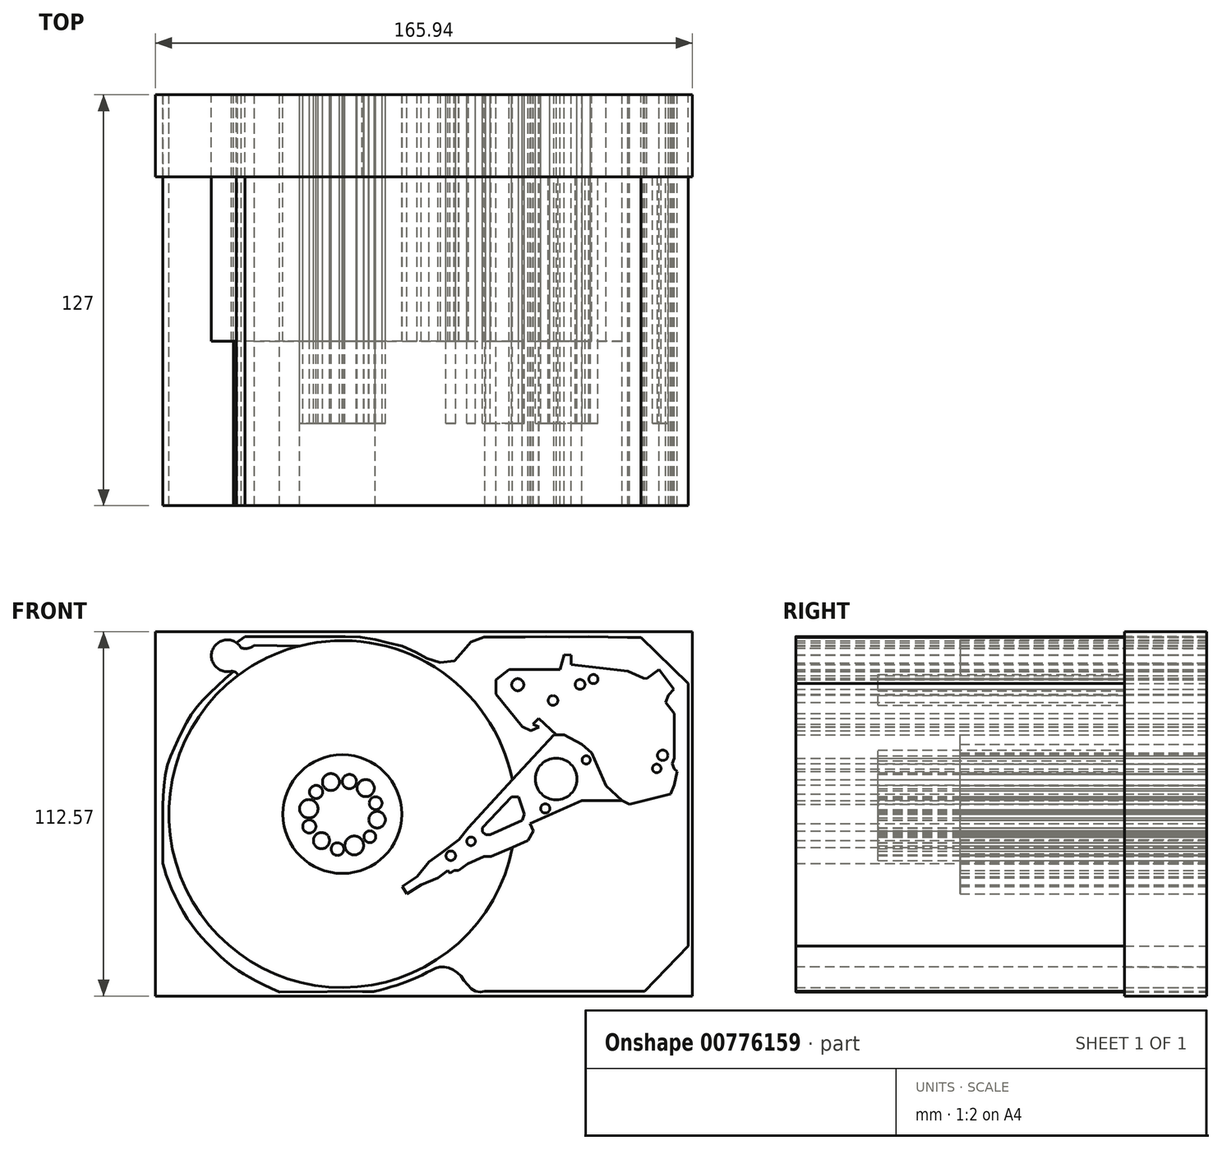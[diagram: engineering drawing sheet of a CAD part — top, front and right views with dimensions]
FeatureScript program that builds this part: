
annotation { "Feature Type Name" : "Feature", "Feature Type Description" : "" }
export const myFeature = defineFeature(function(context is Context, id is Id, definition is map)
    precondition{}
    {
        {
            var Q0;
            Q0=qCreatedBy(makeId("Front.planeOp"),FACE);
            var sketch = newSketch(context, id + "F0", { "sketchPlane" : qUnion([Q0])});
            skLineSegment(sketch, "E0.bottom", {"start": v(-166.9, -0.39) * mm, "end": v(-0.96, -0.39) * mm});
            skLineSegment(sketch, "E0.top", {"start": v(-166.9, -112.96) * mm, "end": v(-0.96, -112.96) * mm});
            skLineSegment(sketch, "E0.right", {"start": v(-0.96, -0.39) * mm, "end": v(-0.96, -112.96) * mm});
            skCircle(sketch, "E1", {"center": v(-109.14, -56.73) * mm, "radius": 53.62 * mm});
            skCircle(sketch, "E2", {"center": v(-109.14, -56.73) * mm, "radius": 18.36 * mm});
            skCircle(sketch, "E3", {"center": v(-144.7, -7.8) * mm, "radius": 2.3 * mm});
            skCircle(sketch, "E4", {"center": v(-144.7, -7.8) * mm, "radius": 4.92 * mm});
            skFitSpline(sketch, "E5", {"points": [v(-143.4, -12.55) * mm, v(-141.85, -13.06) * mm, v(-141.48, -13.95) * mm], "startDerivative": vector(3.27, -0.6) * mm, "endDerivative": vector(0.52, -2.37) * mm});
            skLineSegment(sketch, "E6", {"start": v(-136.28, -4.54) * mm, "end": v(-122.34, -4.75) * mm});
            skFitSpline(sketch, "E7", {"points": [v(-136.28, -4.54) * mm, v(-138.28, -5.49) * mm, v(-140.4, -5.42) * mm], "startDerivative": vector(-3.87, -2.38) * mm, "endDerivative": vector(-4.35, 0.64) * mm});
            skLineSegment(sketch, "E8", {"start": v(-56.57, -46.13) * mm, "end": v(-70.2, -60.97) * mm});
            skLineSegment(sketch, "E9", {"start": v(-70.2, -60.97) * mm, "end": v(-73.07, -64.56) * mm});
            skLineSegment(sketch, "E10", {"start": v(-73.07, -64.56) * mm, "end": v(-78.81, -68.99) * mm});
            skLineSegment(sketch, "E11", {"start": v(-78.81, -68.99) * mm, "end": v(-82.4, -71.5) * mm});
            skLineSegment(sketch, "E12", {"start": v(-82.4, -71.5) * mm, "end": v(-86, -76.05) * mm});
            skLineSegment(sketch, "E13", {"start": v(-86, -76.05) * mm, "end": v(-90.66, -79.04) * mm});
            skLineSegment(sketch, "E14", {"start": v(-90.66, -79.04) * mm, "end": v(-89.15, -81.39) * mm});
            skLineSegment(sketch, "E15", {"start": v(-89.15, -81.39) * mm, "end": v(-84.8, -78.6) * mm});
            skLineSegment(sketch, "E16", {"start": v(-84.8, -78.6) * mm, "end": v(-79.6, -76.39) * mm});
            skLineSegment(sketch, "E17", {"start": v(-79.6, -76.39) * mm, "end": v(-75.84, -73.6) * mm});
            skLineSegment(sketch, "E18", {"start": v(-75.84, -73.6) * mm, "end": v(-70.2, -69) * mm});
            skLineSegment(sketch, "E19", {"start": v(-70.2, -69) * mm, "end": v(-65.06, -66.97) * mm});
            skLineSegment(sketch, "E20", {"start": v(-65.06, -66.97) * mm, "end": v(-63.32, -67.57) * mm});
            skLineSegment(sketch, "E21", {"start": v(-63.32, -67.57) * mm, "end": v(-61.59, -66.81) * mm});
            skLineSegment(sketch, "E22", {"start": v(-61.59, -66.81) * mm, "end": v(-61.59, -65.46) * mm});
            skLineSegment(sketch, "E23", {"start": v(-61.59, -65.46) * mm, "end": v(-55.87, -62.92) * mm});
            skLineSegment(sketch, "E24", {"start": v(-76.54, -74.12) * mm, "end": v(-75.84, -75.07) * mm});
            skLineSegment(sketch, "E25", {"start": v(-75.84, -75.07) * mm, "end": v(-74.56, -74.12) * mm});
            skLineSegment(sketch, "E26", {"start": v(-74.56, -74.12) * mm, "end": v(-73.2, -74.12) * mm});
            skLineSegment(sketch, "E27", {"start": v(-73.2, -74.12) * mm, "end": v(-70.44, -72.08) * mm});
            skLineSegment(sketch, "E28", {"start": v(-70.44, -72.08) * mm, "end": v(-65.36, -69.83) * mm});
            skLineSegment(sketch, "E29", {"start": v(-65.36, -69.83) * mm, "end": v(-63.17, -69.83) * mm});
            skLineSegment(sketch, "E30", {"start": v(-63.17, -69.83) * mm, "end": v(-56.5, -66.97) * mm});
            skCircle(sketch, "E31", {"center": v(-69.35, -65.16) * mm, "radius": 1.33 * mm});
            skCircle(sketch, "E32", {"center": v(-75.6, -69.6) * mm, "radius": 1.49 * mm});
            skLineSegment(sketch, "E33", {"start": v(-65.8, -60.94) * mm, "end": v(-65.8, -62.22) * mm});
            skLineSegment(sketch, "E34", {"start": v(-65.8, -62.22) * mm, "end": v(-64.86, -63.09) * mm});
            skLineSegment(sketch, "E35", {"start": v(-64.86, -63.09) * mm, "end": v(-63.4, -63.09) * mm});
            skLineSegment(sketch, "E36", {"start": v(-63.4, -63.09) * mm, "end": v(-53.52, -58.67) * mm});
            skLineSegment(sketch, "E37", {"start": v(-53.52, -58.67) * mm, "end": v(-52.93, -56.78) * mm});
            skLineSegment(sketch, "E38", {"start": v(-52.93, -56.78) * mm, "end": v(-54.63, -51.36) * mm});
            skLineSegment(sketch, "E39", {"start": v(-54.63, -51.36) * mm, "end": v(-56.84, -51.36) * mm});
            skLineSegment(sketch, "E40", {"start": v(-56.84, -51.36) * mm, "end": v(-65.8, -60.94) * mm});
            skLineSegment(sketch, "E41", {"start": v(-56.5, -66.97) * mm, "end": v(-51.76, -64.87) * mm});
            skLineSegment(sketch, "E42", {"start": v(-51.76, -64.87) * mm, "end": v(-50.07, -61.98) * mm});
            skLineSegment(sketch, "E43", {"start": v(-50.07, -61.98) * mm, "end": v(-51.1, -59.68) * mm});
            skLineSegment(sketch, "E44", {"start": v(-51.1, -59.68) * mm, "end": v(-35.05, -52.56) * mm});
            skLineSegment(sketch, "E45", {"start": v(-35.05, -52.56) * mm, "end": v(-22.63, -52.56) * mm});
            skLineSegment(sketch, "E46", {"start": v(-22.63, -52.56) * mm, "end": v(-27.56, -48.04) * mm});
            skLineSegment(sketch, "E47", {"start": v(-27.56, -48.04) * mm, "end": v(-30.07, -42.36) * mm});
            skLineSegment(sketch, "E48", {"start": v(-30.07, -42.36) * mm, "end": v(-32.1, -37.8) * mm});
            skLineSegment(sketch, "E49", {"start": v(-32.1, -37.8) * mm, "end": v(-35.05, -35.1) * mm});
            skLineSegment(sketch, "E50", {"start": v(-35.05, -35.1) * mm, "end": v(-40.6, -32.18) * mm});
            skLineSegment(sketch, "E51", {"start": v(-40.6, -32.18) * mm, "end": v(-42.98, -32.18) * mm});
            skLineSegment(sketch, "E52", {"start": v(-42.98, -32.18) * mm, "end": v(-50.16, -25.59) * mm});
            skLineSegment(sketch, "E53", {"start": v(-50.16, -25.59) * mm, "end": v(-45, -14.06) * mm});
            skLineSegment(sketch, "E54", {"start": v(-45, -14.06) * mm, "end": v(-42.48, -14.53) * mm});
            skLineSegment(sketch, "E55", {"start": v(-42.48, -14.53) * mm, "end": v(-40.6, -7.44) * mm});
            skLineSegment(sketch, "E56", {"start": v(-40.6, -7.44) * mm, "end": v(-38.38, -7.59) * mm});
            skLineSegment(sketch, "E57", {"start": v(-38.38, -7.59) * mm, "end": v(-38.38, -10.58) * mm});
            skLineSegment(sketch, "E58", {"start": v(-38.38, -10.58) * mm, "end": v(-35.05, -10.95) * mm});
            skLineSegment(sketch, "E59", {"start": v(-35.05, -10.95) * mm, "end": v(-20.88, -12.51) * mm});
            skLineSegment(sketch, "E60", {"start": v(-20.88, -12.51) * mm, "end": v(-17.41, -14.06) * mm});
            skLineSegment(sketch, "E61", {"start": v(-17.41, -14.06) * mm, "end": v(-16.06, -14.67) * mm});
            skLineSegment(sketch, "E62", {"start": v(-16.06, -14.67) * mm, "end": v(-15.01, -14.8) * mm});
            skLineSegment(sketch, "E63", {"start": v(-15.01, -14.8) * mm, "end": v(-11.17, -12) * mm});
            skLineSegment(sketch, "E64", {"start": v(-11.17, -12) * mm, "end": v(-6.7, -18.11) * mm});
            skLineSegment(sketch, "E65", {"start": v(-6.7, -18.11) * mm, "end": v(-8.27, -19.97) * mm});
            skLineSegment(sketch, "E66", {"start": v(-8.27, -19.97) * mm, "end": v(-9.25, -22.16) * mm});
            skLineSegment(sketch, "E67", {"start": v(-9.25, -22.16) * mm, "end": v(-6.48, -25.59) * mm});
            skLineSegment(sketch, "E68", {"start": v(-6.48, -25.59) * mm, "end": v(-6.48, -39.43) * mm});
            skLineSegment(sketch, "E69", {"start": v(-6.48, -39.43) * mm, "end": v(-7.21, -41.08) * mm});
            skLineSegment(sketch, "E70", {"start": v(-7.21, -41.08) * mm, "end": v(-6.48, -42.74) * mm});
            skLineSegment(sketch, "E71", {"start": v(-6.48, -42.74) * mm, "end": v(-5.62, -43.53) * mm});
            skLineSegment(sketch, "E72", {"start": v(-5.62, -43.53) * mm, "end": v(-6.48, -47.71) * mm});
            skLineSegment(sketch, "E73", {"start": v(-6.48, -47.71) * mm, "end": v(-7.71, -50.47) * mm});
            skLineSegment(sketch, "E74", {"start": v(-7.71, -50.47) * mm, "end": v(-20.32, -53.75) * mm});
            skLineSegment(sketch, "E75", {"start": v(-20.32, -53.75) * mm, "end": v(-22.63, -52.56) * mm});
            skLineSegment(sketch, "E76", {"start": v(-48.5, -27.12) * mm, "end": v(-50.16, -28.93) * mm});
            skLineSegment(sketch, "E77", {"start": v(-50.16, -28.93) * mm, "end": v(-48.3, -29.77) * mm});
            skLineSegment(sketch, "E78", {"start": v(-48.3, -29.77) * mm, "end": v(-50.88, -30.91) * mm});
            skLineSegment(sketch, "E79", {"start": v(-50.88, -30.91) * mm, "end": v(-53.52, -29.73) * mm});
            skLineSegment(sketch, "E80", {"start": v(-53.52, -29.73) * mm, "end": v(-61.64, -19.67) * mm});
            skLineSegment(sketch, "E81", {"start": v(-61.64, -19.67) * mm, "end": v(-61.64, -15.24) * mm});
            skLineSegment(sketch, "E82", {"start": v(-61.64, -15.24) * mm, "end": v(-57.63, -12) * mm});
            skLineSegment(sketch, "E83", {"start": v(-57.63, -12) * mm, "end": v(-41.81, -12) * mm});
            skCircle(sketch, "E84", {"center": v(-54.91, -16.75) * mm, "radius": 1.86 * mm});
            skCircle(sketch, "E85", {"center": v(-44, -21.6) * mm, "radius": 1.5 * mm});
            skCircle(sketch, "E86", {"center": v(-35.65, -16.67) * mm, "radius": 1.53 * mm});
            skCircle(sketch, "E87", {"center": v(-31.51, -15) * mm, "radius": 1.42 * mm});
            skCircle(sketch, "E88", {"center": v(-10.1, -38.56) * mm, "radius": 1.62 * mm});
            skCircle(sketch, "E89", {"center": v(-11.93, -42.62) * mm, "radius": 1.32 * mm});
            skCircle(sketch, "E90", {"center": v(-43.03, -45.89) * mm, "radius": 6.45 * mm});
            skCircle(sketch, "E91", {"center": v(-46.4, -55) * mm, "radius": 1.43 * mm});
            skCircle(sketch, "E92", {"center": v(-33.75, -39.98) * mm, "radius": 1.28 * mm});
            skLineSegment(sketch, "E93", {"start": v(-56.57, -46.13) * mm, "end": v(-43.77, -32.18) * mm});
            skFitSpline(sketch, "E94", {"points": [v(-80.33, -11.5) * mm, v(-73.17, -10.43) * mm, v(-69.1, -6.07) * mm, v(-62.2, -5.02) * mm], "startDerivative": vector(23.42, -0.5) * mm, "endDerivative": vector(22.9, -0.58) * mm});
            skLineSegment(sketch, "E95", {"start": v(-62.2, -5.02) * mm, "end": v(-18.18, -5.02) * mm});
            skLineSegment(sketch, "E96", {"start": v(-18.18, -5.02) * mm, "end": v(-4.36, -18.7) * mm});
            skLineSegment(sketch, "E97", {"start": v(-4.36, -18.7) * mm, "end": v(-4.36, -66.47) * mm});
            skFitSpline(sketch, "E98", {"points": [v(-164.6, -71.95) * mm, v(-164.6, -66.7) * mm, v(-164.6, -59.04) * mm, v(-164.6, -51.95) * mm, v(-163.2, -41.7) * mm, v(-160.1, -34.16) * mm, v(-156.17, -26.51) * mm, v(-150.65, -19.87) * mm, v(-142.78, -12.66) * mm], "startDerivative": vector(-0.1, 49.54) * mm, "endDerivative": vector(57.81, 50.96) * mm});
            skFitSpline(sketch, "E99", {"points": [v(-139.28, -1.86) * mm, v(-130.4, -1.86) * mm, v(-117.22, -1.86) * mm, v(-110.36, -1.86) * mm, v(-105.97, -1.86) * mm, v(-100.34, -2.42) * mm, v(-96.51, -3.44) * mm, v(-91.9, -4.45) * mm, v(-87.17, -6.36) * mm, v(-83.68, -8.28) * mm, v(-80.08, -9.63) * mm, v(-75.13, -9.74) * mm, v(-71.98, -6.59) * mm, v(-70.08, -4.18) * mm, v(-67.7, -2.4) * mm, v(-58.27, -2.04) * mm, v(-49.57, -1.92) * mm, v(-38, -2.04) * mm, v(-29.64, -1.92) * mm, v(-20.94, -2.19) * mm, v(-16.12, -1.92) * mm], "startDerivative": vector(136.2, -0.04) * mm, "endDerivative": vector(98.93, 8.93) * mm});
            skLineSegment(sketch, "E100", {"start": v(-20.94, -2.19) * mm, "end": v(-16.78, -2.19) * mm});
            skLineSegment(sketch, "E101", {"start": v(-16.78, -2.19) * mm, "end": v(-2.18, -16.35) * mm});
            skLineSegment(sketch, "E102", {"start": v(-2.18, -16.35) * mm, "end": v(-2.18, -97.56) * mm});
            skLineSegment(sketch, "E103", {"start": v(-2.18, -97.56) * mm, "end": v(-15.7, -111.5) * mm});
            skLineSegment(sketch, "E104", {"start": v(-15.7, -111.5) * mm, "end": v(-65.04, -111.5) * mm});
            skFitSpline(sketch, "E105", {"points": [v(-65.04, -111.5) * mm, v(-67.97, -111.5) * mm, v(-70.81, -109.01) * mm, v(-73.18, -106.08) * mm, v(-75.92, -104.38) * mm, v(-78.87, -103.98) * mm, v(-81.18, -104.78) * mm, v(-84.59, -106.49) * mm, v(-91, -109.2) * mm, v(-94.82, -110.3) * mm, v(-99.01, -111.5) * mm, v(-103.47, -111.5) * mm], "startDerivative": vector(-37.68, -6.43) * mm, "endDerivative": vector(-45.54, 3.55) * mm});
            skLineSegment(sketch, "E106", {"start": v(-99.01, -111.5) * mm, "end": v(-128.6, -111.75) * mm});
            skLineSegment(sketch, "E107", {"start": v(-43.77, -32.18) * mm, "end": v(-42.98, -32.18) * mm});
            skCircle(sketch, "E108", {"center": v(-112.66, -46.82) * mm, "radius": 2.63 * mm});
            skCircle(sketch, "E109", {"center": v(-106.95, -46.67) * mm, "radius": 2.2 * mm});
            skCircle(sketch, "E110", {"center": v(-101.91, -48.7) * mm, "radius": 2.65 * mm});
            skCircle(sketch, "E111", {"center": v(-98.83, -53.36) * mm, "radius": 1.98 * mm});
            skCircle(sketch, "E112", {"center": v(-98.38, -58.47) * mm, "radius": 2.57 * mm});
            skCircle(sketch, "E113", {"center": v(-100.64, -63.73) * mm, "radius": 1.83 * mm});
            skCircle(sketch, "E114", {"center": v(-105.45, -66.43) * mm, "radius": 2.9 * mm});
            skCircle(sketch, "E115", {"center": v(-110.63, -67.56) * mm, "radius": 1.96 * mm});
            skCircle(sketch, "E116", {"center": v(-115.59, -64.93) * mm, "radius": 2.5 * mm});
            skCircle(sketch, "E117", {"center": v(-119.34, -60.57) * mm, "radius": 2.04 * mm});
            skCircle(sketch, "E118", {"center": v(-119.5, -55.09) * mm, "radius": 2.86 * mm});
            skCircle(sketch, "E119", {"center": v(-117.24, -49.9) * mm, "radius": 2.03 * mm});
            skLineSegment(sketch, "E120", {"start": v(-166.9, -0.39) * mm, "end": v(-166.9, -112.96) * mm});
            skLineSegment(sketch, "E121", {"start": v(-143.4, -12.55) * mm, "end": v(-142.78, -12.66) * mm});
            skLineSegment(sketch, "E122", {"start": v(-139.28, -1.86) * mm, "end": v(-141.93, -3.73) * mm});
            skFitSpline(sketch, "E123", {"points": [v(-164.6, -71.95) * mm, v(-162.75, -77.8) * mm, v(-157.8, -87.86) * mm, v(-152.23, -95.23) * mm, v(-143.52, -103.56) * mm, v(-138.11, -107.02) * mm, v(-128.6, -111.75) * mm], "startDerivative": vector(10.62, -39.33) * mm, "endDerivative": vector(57.28, -25) * mm});
            skSolve(sketch);
        }
        {
            var Q0;
            Q0 = qSketchRegion(id + "F0", true);
            extrude(context, id + "F1", {"entities" : qUnion([Q0]), "depth" : 25.4 * mm, "offsetDistance" : 25.4 * mm});
        }
        {
            var Q0;
            Q0=makeQuery(id+"F0.imprint","IMPRINT",FACE,{"disambiguationData":[TD([[makeQuery(id+"F0.imprint","IMPRINT",EDGE,{"derivedFrom":sQuery(id+"F0.wireOp",EDGE,"E2")}),-1.0]])]});
            var Q1;
            Q1=makeQuery(id+"F0.imprint","IMPRINT",FACE,{"disambiguationData":[TD([[makeQuery(id+"F0.imprint","IMPRINT",EDGE,{"derivedFrom":sQuery(id+"F0.wireOp",EDGE,"HnRhpPPG-Nzn8-Kiqb-eVUc-xORakVnLolAv")}),1.0]])]});
            var Q2;
            Q2=makeQuery(id+"F0.imprint","IMPRINT",FACE,{"disambiguationData":[TD([[makeQuery(id+"F0.imprint","IMPRINT",EDGE,{"derivedFrom":sQuery(id+"F0.wireOp",EDGE,"E46")}),-1.0]])]});
            var Q3;
            {var subQ3=sQuery(id+"F0.wireOp",EDGE,"E53");Q3=makeQuery(id+"F0.imprint","IMPRINT",FACE,{"disambiguationData":[TD([[makeQuery(id+"F0.imprint","IMPRINT",EDGE,{"derivedFrom":subQ3}),1.0]])]});}
            extrude(context, id + "F2", {"entities" : qUnion([Q0, Q1, Q2, Q3]), "operationType" : NewBodyOperationType.ADD, "depth" : 25.4 * mm, "offsetDistance" : 25.4 * mm});
        }
        {
            var Q0;
            Q0=makeQuery(id+"F0.imprint","IMPRINT",FACE,{"disambiguationData":[TD([[makeQuery(id+"F0.imprint","IMPRINT",EDGE,{"derivedFrom":sQuery(id+"F0.wireOp",EDGE,"E117")}),1.0]])]});
            var Q1;
            Q1=makeQuery(id+"F0.imprint","IMPRINT",FACE,{"disambiguationData":[TD([[makeQuery(id+"F0.imprint","IMPRINT",EDGE,{"derivedFrom":sQuery(id+"F0.wireOp",EDGE,"E118")}),1.0]])]});
            var Q2;
            Q2=makeQuery(id+"F0.imprint","IMPRINT",FACE,{"disambiguationData":[TD([[makeQuery(id+"F0.imprint","IMPRINT",EDGE,{"derivedFrom":sQuery(id+"F0.wireOp",EDGE,"E119")}),1.0]])]});
            var Q3;
            Q3=makeQuery(id+"F0.imprint","IMPRINT",FACE,{"disambiguationData":[TD([[makeQuery(id+"F0.imprint","IMPRINT",EDGE,{"derivedFrom":sQuery(id+"F0.wireOp",EDGE,"E108")}),1.0]])]});
            var Q4;
            Q4=makeQuery(id+"F0.imprint","IMPRINT",FACE,{"disambiguationData":[TD([[makeQuery(id+"F0.imprint","IMPRINT",EDGE,{"derivedFrom":sQuery(id+"F0.wireOp",EDGE,"E109")}),1.0]])]});
            var Q5;
            Q5=makeQuery(id+"F0.imprint","IMPRINT",FACE,{"disambiguationData":[TD([[makeQuery(id+"F0.imprint","IMPRINT",EDGE,{"derivedFrom":sQuery(id+"F0.wireOp",EDGE,"E110")}),1.0]])]});
            var Q6;
            Q6=makeQuery(id+"F0.imprint","IMPRINT",FACE,{"disambiguationData":[TD([[makeQuery(id+"F0.imprint","IMPRINT",EDGE,{"derivedFrom":sQuery(id+"F0.wireOp",EDGE,"E111")}),1.0]])]});
            var Q7;
            Q7=makeQuery(id+"F0.imprint","IMPRINT",FACE,{"disambiguationData":[TD([[makeQuery(id+"F0.imprint","IMPRINT",EDGE,{"derivedFrom":sQuery(id+"F0.wireOp",EDGE,"E112")}),1.0]])]});
            var Q8;
            Q8=makeQuery(id+"F0.imprint","IMPRINT",FACE,{"disambiguationData":[TD([[makeQuery(id+"F0.imprint","IMPRINT",EDGE,{"derivedFrom":sQuery(id+"F0.wireOp",EDGE,"E113")}),1.0]])]});
            var Q9;
            Q9=makeQuery(id+"F0.imprint","IMPRINT",FACE,{"disambiguationData":[TD([[makeQuery(id+"F0.imprint","IMPRINT",EDGE,{"derivedFrom":sQuery(id+"F0.wireOp",EDGE,"E114")}),1.0]])]});
            var Q10;
            Q10=makeQuery(id+"F0.imprint","IMPRINT",FACE,{"disambiguationData":[TD([[makeQuery(id+"F0.imprint","IMPRINT",EDGE,{"derivedFrom":sQuery(id+"F0.wireOp",EDGE,"E115")}),1.0]])]});
            var Q11;
            Q11=makeQuery(id+"F0.imprint","IMPRINT",FACE,{"disambiguationData":[TD([[makeQuery(id+"F0.imprint","IMPRINT",EDGE,{"derivedFrom":sQuery(id+"F0.wireOp",EDGE,"E116")}),1.0]])]});
            var Q12;
            Q12=makeQuery(id+"F0.imprint","IMPRINT",FACE,{"disambiguationData":[TD([[makeQuery(id+"F0.imprint","IMPRINT",EDGE,{"derivedFrom":sQuery(id+"F0.wireOp",EDGE,"E33")}),1.0]])]});
            var Q13;
            {var subQ1=sQuery(id+"F0.wireOp",EDGE,"E37");Q13=makeQuery(id+"F0.imprint","IMPRINT",FACE,{"disambiguationData":[TD([[makeQuery(id+"F0.imprint","IMPRINT",EDGE,{"derivedFrom":subQ1}),1.0]])]});}
            var Q14;
            Q14=makeQuery(id+"F0.imprint","IMPRINT",FACE,{"disambiguationData":[TD([[makeQuery(id+"F0.imprint","IMPRINT",EDGE,{"derivedFrom":sQuery(id+"F0.wireOp",EDGE,"E91")}),1.0]])]});
            var Q15;
            Q15=makeQuery(id+"F0.imprint","IMPRINT",FACE,{"disambiguationData":[TD([[makeQuery(id+"F0.imprint","IMPRINT",EDGE,{"derivedFrom":sQuery(id+"F0.wireOp",EDGE,"E90")}),1.0]])]});
            var Q16;
            Q16=makeQuery(id+"F0.imprint","IMPRINT",FACE,{"disambiguationData":[TD([[makeQuery(id+"F0.imprint","IMPRINT",EDGE,{"derivedFrom":sQuery(id+"F0.wireOp",EDGE,"E92")}),1.0]])]});
            var Q17;
            Q17=makeQuery(id+"F0.imprint","IMPRINT",FACE,{"disambiguationData":[TD([[makeQuery(id+"F0.imprint","IMPRINT",EDGE,{"derivedFrom":sQuery(id+"F0.wireOp",EDGE,"E32")}),1.0]])]});
            var Q18;
            Q18=makeQuery(id+"F0.imprint","IMPRINT",FACE,{"disambiguationData":[TD([[makeQuery(id+"F0.imprint","IMPRINT",EDGE,{"derivedFrom":sQuery(id+"F0.wireOp",EDGE,"E31")}),1.0]])]});
            var Q19;
            Q19=makeQuery(id+"F0.imprint","IMPRINT",FACE,{"disambiguationData":[TD([[makeQuery(id+"F0.imprint","IMPRINT",EDGE,{"derivedFrom":sQuery(id+"F0.wireOp",EDGE,"E84")}),1.0]])]});
            var Q20;
            Q20=makeQuery(id+"F0.imprint","IMPRINT",FACE,{"disambiguationData":[TD([[makeQuery(id+"F0.imprint","IMPRINT",EDGE,{"derivedFrom":sQuery(id+"F0.wireOp",EDGE,"E85")}),1.0]])]});
            var Q21;
            Q21=makeQuery(id+"F0.imprint","IMPRINT",FACE,{"disambiguationData":[TD([[makeQuery(id+"F0.imprint","IMPRINT",EDGE,{"derivedFrom":sQuery(id+"F0.wireOp",EDGE,"E86")}),1.0]])]});
            var Q22;
            Q22=makeQuery(id+"F0.imprint","IMPRINT",FACE,{"disambiguationData":[TD([[makeQuery(id+"F0.imprint","IMPRINT",EDGE,{"derivedFrom":sQuery(id+"F0.wireOp",EDGE,"E87")}),1.0]])]});
            var Q23;
            Q23=makeQuery(id+"F0.imprint","IMPRINT",FACE,{"disambiguationData":[TD([[makeQuery(id+"F0.imprint","IMPRINT",EDGE,{"derivedFrom":sQuery(id+"F0.wireOp",EDGE,"E88")}),1.0]])]});
            var Q24;
            Q24=makeQuery(id+"F0.imprint","IMPRINT",FACE,{"disambiguationData":[TD([[makeQuery(id+"F0.imprint","IMPRINT",EDGE,{"derivedFrom":sQuery(id+"F0.wireOp",EDGE,"E89")}),1.0]])]});
            extrude(context, id + "F3", {"entities" : qUnion([Q0, Q1, Q2, Q3, Q4, Q5, Q6, Q7, Q8, Q9, Q10, Q11, Q12, Q13, Q14, Q15, Q16, Q17, Q18, Q19, Q20, Q21, Q22, Q23, Q24]), "operationType" : NewBodyOperationType.ADD, "depth" : 101.6 * mm, "offsetDistance" : 25.4 * mm});
        }
        {
            var Q0;
            Q0=makeQuery(id+"F0.imprint","IMPRINT",FACE,{"disambiguationData":[TD([[makeQuery(id+"F0.imprint","IMPRINT",EDGE,{"derivedFrom":sQuery(id+"F0.wireOp",EDGE,"E2")}),1.0]])]});
            var Q1;
            {var subQ1=sQuery(id+"F0.wireOp",EDGE,"E37");Q1=makeQuery(id+"F0.imprint","IMPRINT",FACE,{"disambiguationData":[TD([[makeQuery(id+"F0.imprint","IMPRINT",EDGE,{"derivedFrom":subQ1}),-1.0]])]});}
            var Q2;
            {var subQ5=sQuery(id+"F0.wireOp",EDGE,"E8");Q2=makeQuery(id+"F0.imprint","IMPRINT",FACE,{"disambiguationData":[TD([[makeQuery(id+"F0.imprint","IMPRINT",EDGE,{"derivedFrom":subQ5}),1.0]])]});}
            var Q3;
            {var subQ4=sQuery(id+"F0.wireOp",EDGE,"E18");Q3=makeQuery(id+"F0.imprint","IMPRINT",FACE,{"disambiguationData":[TD([[makeQuery(id+"F0.imprint","IMPRINT",EDGE,{"derivedFrom":subQ4}),-1.0]])]});}
            var Q4;
            {var subQ0=sQuery(id+"F0.wireOp",EDGE,"E6");Q4=makeQuery(id+"F0.imprint","IMPRINT",FACE,{"disambiguationData":[TD([[makeQuery(id+"F0.imprint","IMPRINT",EDGE,{"derivedFrom":subQ0}),-1.0]])]});}
            var Q5;
            Q5=makeQuery(id+"F0.imprint","IMPRINT",FACE,{"disambiguationData":[TD([[makeQuery(id+"F0.imprint","IMPRINT",EDGE,{"derivedFrom":sQuery(id+"F0.wireOp",EDGE,"E3")}),-1.0]])]});
            var Q6;
            Q6=makeQuery(id+"F0.imprint","IMPRINT",FACE,{"disambiguationData":[TD([[makeQuery(id+"F0.imprint","IMPRINT",EDGE,{"derivedFrom":sQuery(id+"F0.wireOp",EDGE,"E3")}),1.0]])]});
            extrude(context, id + "F4", {"entities" : qUnion([Q0, Q1, Q2, Q3, Q4, Q5, Q6]), "depth" : 76.2 * mm, "offsetDistance" : 25.4 * mm});
        }
        {
            var Q0;
            {var subQ14=sQuery(id+"F0.wireOp",EDGE,"E6");Q0=makeQuery(id+"F0.imprint","IMPRINT",FACE,{"disambiguationData":[TD([[makeQuery(id+"F0.imprint","IMPRINT",EDGE,{"derivedFrom":subQ14}),1.0]])]});}
            extrude(context, id + "F5", {"entities" : qUnion([Q0]), "depth" : 127 * mm, "offsetDistance" : 25.4 * mm});
        }
    });
